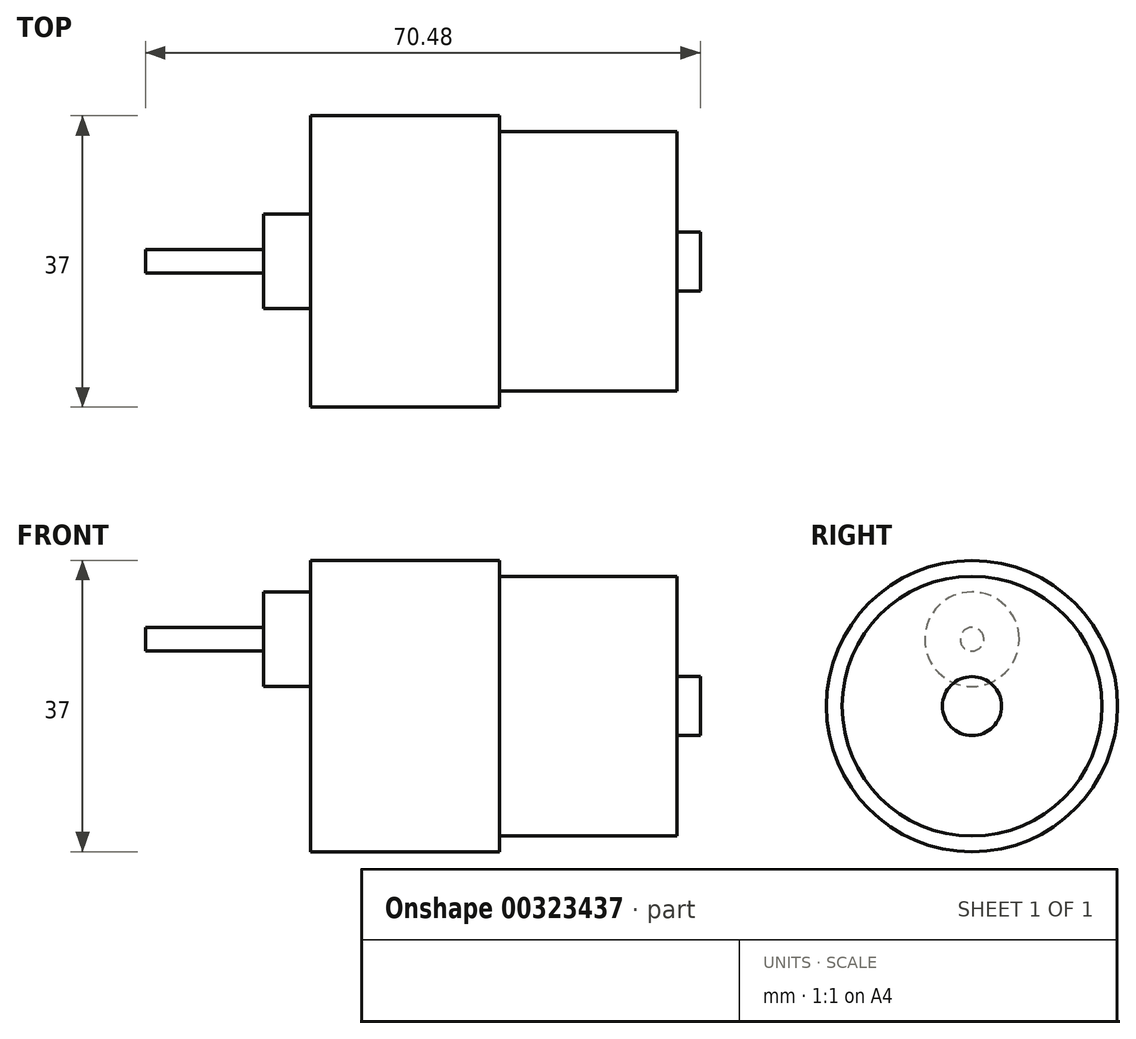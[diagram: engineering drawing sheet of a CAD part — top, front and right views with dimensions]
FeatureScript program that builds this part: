
annotation { "Feature Type Name" : "Feature", "Feature Type Description" : "" }
export const myFeature = defineFeature(function(context is Context, id is Id, definition is map)
    precondition{}
    {
        {
            var Q0;
            Q0=qCreatedBy(makeId("Front.planeOp"),FACE);
            var sketch = newSketch(context, id + "F0", { "sketchPlane" : qUnion([Q0])});
            skLineSegment(sketch, "E0", {"start": v(-24, 0) * mm, "end": v(-24, 18.5) * mm});
            skLineSegment(sketch, "E1", {"start": v(0, 18.5) * mm, "end": v(0, 0) * mm});
            skLineSegment(sketch, "E2", {"start": v(0, 0) * mm, "end": v(-24, 0) * mm});
            skLineSegment(sketch, "E3", {"start": v(-24, 18.5) * mm, "end": v(0, 18.5) * mm});
            skLineSegment(sketch, "E4", {"start": v(-35.56, 0) * mm, "end": v(15.21, 0) * mm, "construction": true});
            skSolve(sketch);
        }
        {
            var Q0;
            Q0=makeQuery(id+"F0.imprint","IMPRINT",FACE,{"disambiguationData":[TD([[makeQuery(id+"F0.imprint","IMPRINT",EDGE,{"derivedFrom":sQuery(id+"F0.wireOp",EDGE,"E0")}),-1.0]])]});
            var Q1;
            Q1=sQuery(id+"F0.wireOp",EDGE,"E4");
            revolve(context, id + "F1", {"entities" : qUnion([Q0]), "axis" : qUnion([Q1]), "revolveType" : RevolveType.FULL});
        }
        {
            var Q0;
            Q0=qCreatedBy(makeId("Front.planeOp"),FACE);
            var sketch = newSketch(context, id + "F2", { "sketchPlane" : qUnion([Q0])});
            skLineSegment(sketch, "E5", {"start": v(-18.77, 0) * mm, "end": v(27.67, 0) * mm, "construction": true});
            skLineSegment(sketch, "E6.bottom", {"start": v(0, 0) * mm, "end": v(19.5, 0) * mm});
            skLineSegment(sketch, "E6.top", {"start": v(0, 16.5) * mm, "end": v(19.5, 16.5) * mm});
            skLineSegment(sketch, "E6.left", {"start": v(0, 0) * mm, "end": v(0, 16.5) * mm});
            skLineSegment(sketch, "E6.right", {"start": v(19.5, 0) * mm, "end": v(19.5, 16.5) * mm});
            skSolve(sketch);
        }
        {
            var Q0;
            Q0 = qSketchRegion(id + "F2", true);
            var Q1;
            Q1=sQuery(id+"F2.wireOp",EDGE,"E5");
            revolve(context, id + "F3", {"operationType" : NewBodyOperationType.ADD, "entities" : qUnion([Q0]), "axis" : qUnion([Q1]), "revolveType" : RevolveType.FULL});
        }
        {
            var Q0;
            Q0=qCreatedBy(makeId("Front.planeOp"),FACE);
            var sketch = newSketch(context, id + "F4", { "sketchPlane" : qUnion([Q0])});
            skLineSegment(sketch, "E7.bottom", {"start": v(19.5, 16.5) * mm, "end": v(22.5, 16.5) * mm});
            skLineSegment(sketch, "E7.top", {"start": v(19.5, 0) * mm, "end": v(22.5, 0) * mm});
            skLineSegment(sketch, "E7.left", {"start": v(19.5, 16.5) * mm, "end": v(19.5, 0) * mm});
            skLineSegment(sketch, "E7.right", {"start": v(22.5, 16.5) * mm, "end": v(22.5, 0) * mm});
            skLineSegment(sketch, "E8", {"start": v(27.95, 0) * mm, "end": v(16.3, 0) * mm, "construction": true});
            skSolve(sketch);
        }
        {
            var Q0;
            Q0 = qSketchRegion(id + "F4", true);
            var Q1;
            Q1=sQuery(id+"F4.wireOp",EDGE,"E8");
            revolve(context, id + "F5", {"operationType" : NewBodyOperationType.ADD, "entities" : qUnion([Q0]), "axis" : qUnion([Q1]), "revolveType" : RevolveType.FULL});
        }
        {
            var Q0;
            Q0=qCreatedBy(makeId("Front.planeOp"),FACE);
            var sketch = newSketch(context, id + "F6", { "sketchPlane" : qUnion([Q0])});
            skLineSegment(sketch, "E9.bottom", {"start": v(22.5, 3.75) * mm, "end": v(25.5, 3.75) * mm});
            skLineSegment(sketch, "E9.top", {"start": v(22.5, 0) * mm, "end": v(25.5, 0) * mm});
            skLineSegment(sketch, "E9.left", {"start": v(22.5, 3.75) * mm, "end": v(22.5, 0) * mm});
            skLineSegment(sketch, "E9.right", {"start": v(25.5, 3.75) * mm, "end": v(25.5, 0) * mm});
            skLineSegment(sketch, "E10", {"start": v(-27.72, 0) * mm, "end": v(29.74, 0) * mm, "construction": true});
            skSolve(sketch);
        }
        {
            var Q0;
            Q0=makeQuery(id+"F6.imprint","IMPRINT",FACE,{"disambiguationData":[TD([[makeQuery(id+"F6.imprint","IMPRINT",EDGE,{"derivedFrom":sQuery(id+"F6.wireOp",EDGE,"E9.bottom")}),-1.0]])]});
            var Q1;
            Q1=sQuery(id+"F6.wireOp",EDGE,"E10");
            revolve(context, id + "F7", {"operationType" : NewBodyOperationType.ADD, "entities" : qUnion([Q0]), "axis" : qUnion([Q1]), "revolveType" : RevolveType.FULL});
        }
        {
            var Q0;
            Q0=qCreatedBy(makeId("Front.planeOp"),FACE);
            var sketch = newSketch(context, id + "F8", { "sketchPlane" : qUnion([Q0])});
            skLineSegment(sketch, "E11", {"start": v(-42.04, 8.5) * mm, "end": v(29.05, 8.5) * mm, "construction": true});
            skLineSegment(sketch, "E12.bottom", {"start": v(-29.97, 14.5) * mm, "end": v(-23.97, 14.5) * mm});
            skLineSegment(sketch, "E12.top", {"start": v(-29.97, 8.5) * mm, "end": v(-23.97, 8.5) * mm});
            skLineSegment(sketch, "E12.left", {"start": v(-29.97, 14.5) * mm, "end": v(-29.97, 8.5) * mm});
            skLineSegment(sketch, "E12.right", {"start": v(-23.97, 14.5) * mm, "end": v(-23.97, 8.5) * mm});
            skSolve(sketch);
        }
        {
            var Q0;
            Q0=makeQuery(id+"F8.imprint","IMPRINT",FACE,{"disambiguationData":[TD([[makeQuery(id+"F8.imprint","IMPRINT",EDGE,{"derivedFrom":sQuery(id+"F8.wireOp",EDGE,"E12.bottom")}),-1.0]])]});
            var Q1;
            Q1=sQuery(id+"F8.wireOp",EDGE,"E11");
            revolve(context, id + "F9", {"operationType" : NewBodyOperationType.ADD, "entities" : qUnion([Q0]), "axis" : qUnion([Q1]), "revolveType" : RevolveType.FULL});
        }
        {
            var Q0;
            Q0=qCreatedBy(makeId("Front.planeOp"),FACE);
            var sketch = newSketch(context, id + "F10", { "sketchPlane" : qUnion([Q0])});
            skLineSegment(sketch, "E13", {"start": v(-48.47, 8.5) * mm, "end": v(23.39, 8.5) * mm, "construction": true});
            skLineSegment(sketch, "E14.bottom", {"start": v(-44.98, 10) * mm, "end": v(-29.98, 10) * mm});
            skLineSegment(sketch, "E14.top", {"start": v(-44.98, 8.5) * mm, "end": v(-29.98, 8.5) * mm});
            skLineSegment(sketch, "E14.left", {"start": v(-44.98, 10) * mm, "end": v(-44.98, 8.5) * mm});
            skLineSegment(sketch, "E14.right", {"start": v(-29.98, 10) * mm, "end": v(-29.98, 8.5) * mm});
            skSolve(sketch);
        }
        {
            var Q0;
            Q0=makeQuery(id+"F10.imprint","IMPRINT",FACE,{"disambiguationData":[TD([[makeQuery(id+"F10.imprint","IMPRINT",EDGE,{"derivedFrom":sQuery(id+"F10.wireOp",EDGE,"E14.bottom")}),-1.0]])]});
            var Q1;
            Q1=sQuery(id+"F10.wireOp",EDGE,"E13");
            revolve(context, id + "F11", {"entities" : qUnion([Q0]), "axis" : qUnion([Q1]), "revolveType" : RevolveType.FULL});
        }
    });
